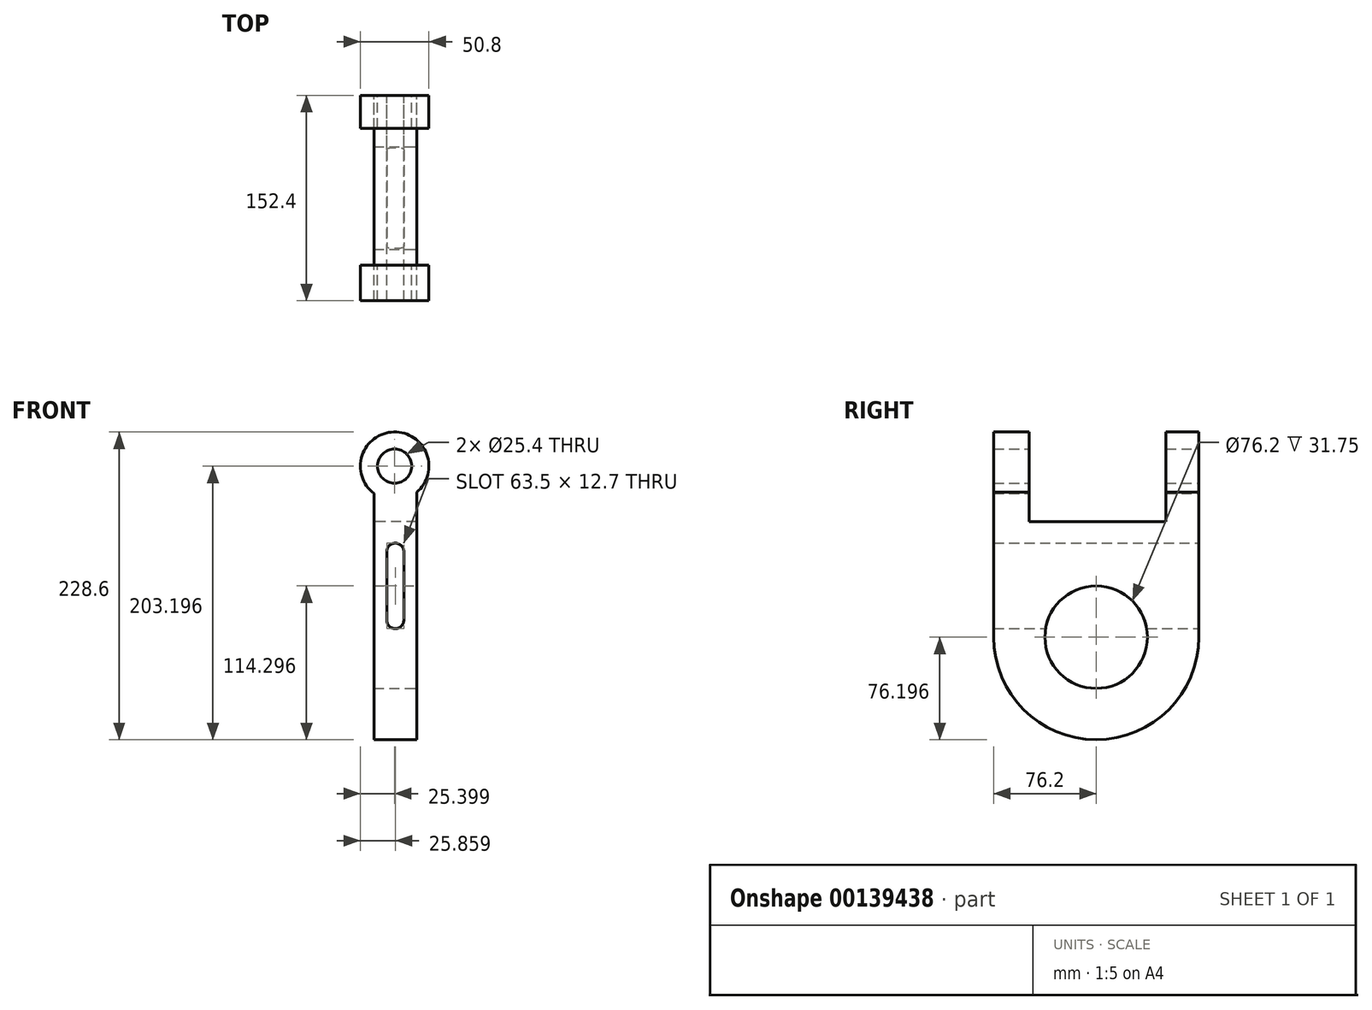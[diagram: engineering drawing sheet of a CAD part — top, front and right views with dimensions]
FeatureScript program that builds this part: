
annotation { "Feature Type Name" : "Feature", "Feature Type Description" : "" }
export const myFeature = defineFeature(function(context is Context, id is Id, definition is map)
    precondition{}
    {
        {
            var Q0;
            Q0=qCreatedBy(makeId("Front.planeOp"),FACE);
            var sketch = newSketch(context, id + "F0", { "sketchPlane" : qUnion([Q0])});
            skArc(sketch, "E0", {"start": v(-39.08, 42.03) * mm, "mid": v(-56, 86.87) * mm, "end": v(-70.83, 41.29) * mm});
            skCircle(sketch, "E1", {"center": v(-55.41, 61.48) * mm, "radius": 12.7 * mm});
            skLineSegment(sketch, "E2", {"start": v(-70.83, 41.29) * mm, "end": v(-70.83, -141.72) * mm});
            skLineSegment(sketch, "E3", {"start": v(-39.08, 42.03) * mm, "end": v(-39.08, -141.72) * mm});
            skLineSegment(sketch, "E4", {"start": v(-39.08, -141.72) * mm, "end": v(-70.83, -141.72) * mm});
            skLineSegment(sketch, "E5", {"start": v(-61.3, -2.02) * mm, "end": v(-61.3, -52.82) * mm});
            skLineSegment(sketch, "E6", {"start": v(-48.6, -2.02) * mm, "end": v(-48.6, -52.82) * mm});
            skArc(sketch, "E7", {"start": v(-48.6, -2.02) * mm, "mid": v(-54.95, 4.33) * mm, "end": v(-61.3, -2.02) * mm});
            skArc(sketch, "E8", {"start": v(-61.3, -52.82) * mm, "mid": v(-54.95, -59.17) * mm, "end": v(-48.6, -52.82) * mm});
            skSolve(sketch);
        }
        {
            var Q0;
            Q0=makeQuery(id+"F0.imprint","IMPRINT",FACE,{"disambiguationData":[TD([[makeQuery(id+"F0.imprint","IMPRINT",EDGE,{"derivedFrom":sQuery(id+"F0.wireOp",EDGE,"E0")}),1.0]])]});
            var Q1;
            Q1=makeQuery(id+"F0.imprint","IMPRINT",FACE,{"disambiguationData":[TD([[makeQuery(id+"F0.imprint","IMPRINT",EDGE,{"derivedFrom":sQuery(id+"F0.wireOp",EDGE,"E5")}),1.0]])]});
            extrude(context, id + "F1", {"entities" : qUnion([Q0, Q1]), "depth" : 152.4 * mm});
        }
        {
            var Q0;
            Q0=makeQuery(id+"F1.opExtrude","CAP_EDGE",EDGE,{"disambiguationData":[OSD([sQuery(id+"F0.wireOp",EDGE,"E4")])],"isStart":true});
            var Q1;
            Q1=makeQuery(id+"F1.opExtrude","CAP_EDGE",EDGE,{"disambiguationData":[OSD([sQuery(id+"F0.wireOp",EDGE,"E4")])],"isStart":false});
            fillet(context, id + "F2", {"entities" : qUnion([Q0, Q1]), "radius" : 76.2 * mm, "tangentPropagation" : true, "allowEdgeOverflow" : false});
        }
        {
            var Q0;
            Q0=makeQuery(id+"F1.opExtrude","SWEPT_FACE",FACE,{"disambiguationData":[OSD([sQuery(id+"F0.wireOp",EDGE,"E3")])]});
            var sketch = newSketch(context, id + "F3", { "sketchPlane" : qUnion([Q0])});
            skCircle(sketch, "E9", {"center": v(-76.2, -65.52) * mm, "radius": 38.1 * mm});
            skSolve(sketch);
        }
        {
            var Q0;
            Q0=makeQuery(id+"F3.imprint","IMPRINT",FACE,{"disambiguationData":[TD([[makeQuery(id+"F3.imprint","IMPRINT",EDGE,{"derivedFrom":sQuery(id+"F3.wireOp",EDGE,"E9")}),1.0]])]});
            extrude(context, id + "F4", {"entities" : qUnion([Q0]), "operationType" : NewBodyOperationType.REMOVE, "endBound" : BoundingType.THROUGH_ALL, "oppositeDirection" : true, "depth" : 25.4 * mm});
        }
        {
            var Q0;
            Q0=qCreatedBy(makeId("Right.planeOp"),FACE);
            cPlane(context, id + "F5", {"entities" : qUnion([Q0]), "cplaneType" : CPlaneType.OFFSET, "offset" : 127 * mm, "oppositeDirection" : true, "width" : 152.4 * mm, "height" : 152.4 * mm});
        }
        {
            var Q0;
            Q0=qCreatedBy(id+"F5.planeOp",FACE);
            var sketch = newSketch(context, id + "F6", { "sketchPlane" : qUnion([Q0])});
            skLineSegment(sketch, "E10", {"start": v(-125.9, 96.47) * mm, "end": v(-125.9, 20.27) * mm});
            skLineSegment(sketch, "E11", {"start": v(-125.9, 20.27) * mm, "end": v(-24.3, 20.27) * mm});
            skLineSegment(sketch, "E12", {"start": v(-24.3, 20.27) * mm, "end": v(-24.3, 100.4) * mm});
            skLineSegment(sketch, "E13", {"start": v(-24.3, 100.4) * mm, "end": v(-125.9, 96.47) * mm});
            skSolve(sketch);
        }
        {
            var Q0;
            Q0=makeQuery(id+"F6.imprint","IMPRINT",FACE,{"disambiguationData":[TD([[makeQuery(id+"F6.imprint","IMPRINT",EDGE,{"derivedFrom":sQuery(id+"F6.wireOp",EDGE,"E10")}),1.0]])]});
            extrude(context, id + "F7", {"entities" : qUnion([Q0]), "operationType" : NewBodyOperationType.REMOVE, "endBound" : BoundingType.THROUGH_ALL, "depth" : 25.4 * mm});
        }
        {
            var Q0;
            Q0=makeQuery(id+"F0.imprint","IMPRINT",FACE,{"disambiguationData":[TD([[makeQuery(id+"F0.imprint","IMPRINT",EDGE,{"derivedFrom":sQuery(id+"F0.wireOp",EDGE,"E5")}),1.0]])]});
            extrude(context, id + "F8", {"entities" : qUnion([Q0]), "operationType" : NewBodyOperationType.REMOVE, "endBound" : BoundingType.THROUGH_ALL, "depth" : 25.4 * mm});
        }
    });
